# Revit family: 206_VAL-P-_ for OKE
name_source: partatom
category: Duct Accessories
units: mm (PartAtom-declared; Revit-internal decimal feet)

## family parameters
Always vertical = Yes
Cut with Voids When Loaded = No
Part Type = Breaks Into
Round Connector Dimension = Use Diameter
Shared = No
Work Plane-Based = No

## types (4) — shared parameters
CAT0 = Yes
CL = 50 mm  [stored 0.164042 ft]
CL__ve = -50 mm  [stored -0.164042 ft]
Description = Plenum sound attenuator
H1 = 2 mm  [stored 0.00656168 ft]
H1__ve = -2 mm  [stored -0.00656168 ft]
L2D = 50 mm  [stored 0.164042 ft]
Manufacturer = Climecon
QmdConnectorList = 201;D;202;CLD
URL = www.climecon.fi
magiPartTypeId = 206
magiProductFamilyId = VAL-P-* for OKE
zero-valued in all types: MC_Default_elevation

## per-type parameters (varying)
| type | A1 | A2 | AA | B | B1 | CLD | CX | D | E1 | E2 | E2__ve | F | H2D | K1 | W2D |
| VAL-P-100 for OKE | 290 mm  [stored 0.951444 ft] | 280 mm  [stored 0.918635 ft] | 140 mm  [stored 0.459318 ft] | 200 mm  [stored 0.656168 ft] | 190 mm  [stored 0.62336 ft] | 100 mm | 50 mm  [stored 0.164042 ft] | 100 mm | 150 mm  [stored 0.492126 ft] | 146 mm  [stored 0.479003 ft] | -146 mm  [stored -0.479003 ft] | 90 mm  [stored 0.295276 ft] | 100 mm  [stored 0.328084 ft] | 45 mm  [stored 0.147638 ft] | 100 mm  [stored 0.328084 ft] |
| VAL-P-200 for OKE | 440 mm | 430 mm | 215 mm  [stored 0.705381 ft] | 300 mm  [stored 0.984252 ft] | 290 mm  [stored 0.951444 ft] | 200 mm | 100 mm  [stored 0.328084 ft] | 200 mm | 250 mm  [stored 0.82021 ft] | 246 mm  [stored 0.807087 ft] | -246 mm  [stored -0.807087 ft] | 140 mm  [stored 0.459318 ft] | 200 mm  [stored 0.656168 ft] | 70 mm  [stored 0.229659 ft] | 200 mm  [stored 0.656168 ft] |
| VAL-P-160 for OKE | 380 mm | 370 mm | 185 mm  [stored 0.606955 ft] | 260 mm  [stored 0.853018 ft] | 250 mm  [stored 0.82021 ft] | 160 mm | 80 mm  [stored 0.262467 ft] | 160 mm | 210 mm  [stored 0.688976 ft] | 206 mm  [stored 0.675853 ft] | -206 mm  [stored -0.675853 ft] | 120 mm  [stored 0.393701 ft] | 160 mm  [stored 0.524934 ft] | 60 mm  [stored 0.19685 ft] | 160 mm  [stored 0.524934 ft] |
| VAL-P-125 for OKE | 330 mm  [stored 1.08268 ft] | 320 mm  [stored 1.04987 ft] | 160 mm  [stored 0.524934 ft] | 230 mm  [stored 0.754593 ft] | 220 mm  [stored 0.721785 ft] | 125 mm | 63 mm | 125 mm | 175 mm  [stored 0.574147 ft] | 171 mm  [stored 0.561024 ft] | -171 mm  [stored -0.561024 ft] | 100 mm  [stored 0.328084 ft] | 125 mm  [stored 0.410105 ft] | 50 mm  [stored 0.164042 ft] | 125 mm  [stored 0.410105 ft] |

note: column(s) folded — value = type name in every type: magiProductCode, magiProductId

note: [stored X ft] marks values corroborated as IEEE doubles in the binary element streams (Revit-internal decimal feet)

## geometry (parser evidence)
native form markers: Sweep x2
no freeform markers — native parametric forms only
